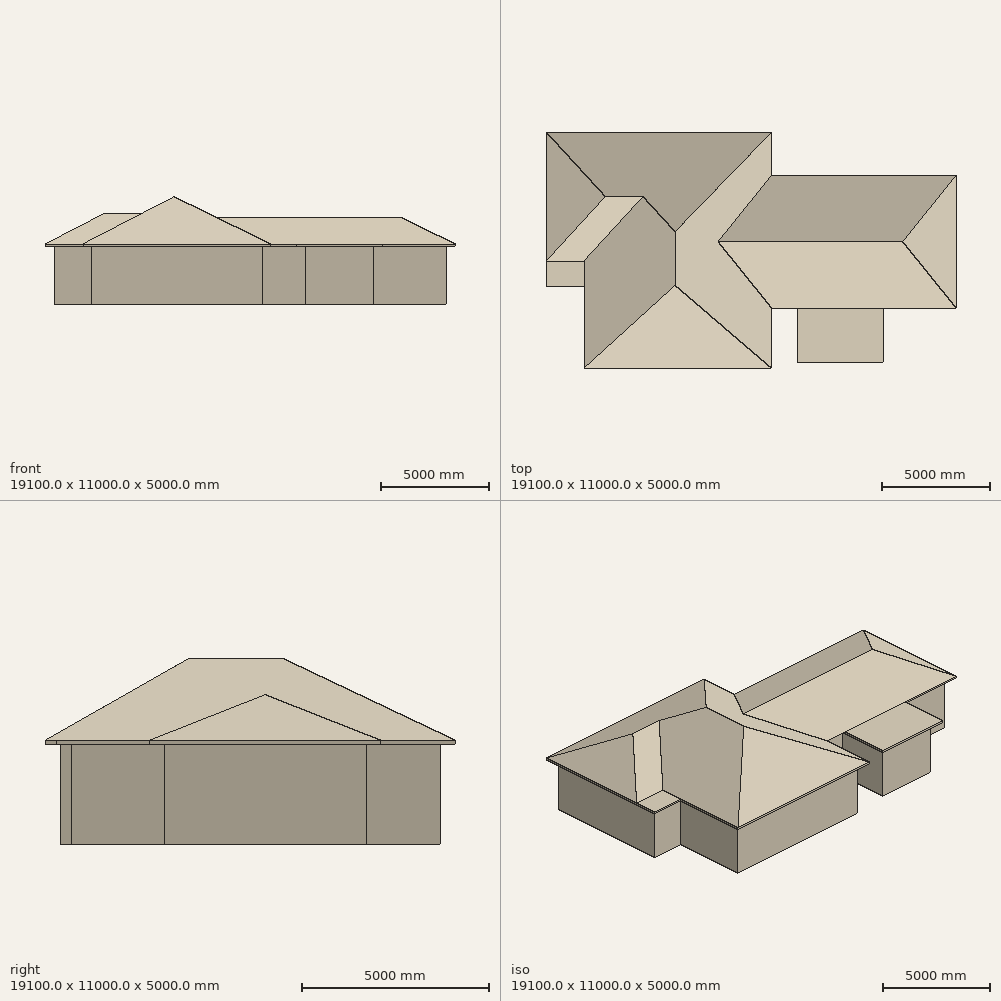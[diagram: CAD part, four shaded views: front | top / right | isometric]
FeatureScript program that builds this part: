
annotation { "Feature Type Name" : "Feature", "Feature Type Description" : "" }
export const myFeature = defineFeature(function(context is Context, id is Id, definition is map)
    precondition{}
    {
        {
            var Q0;
            Q0=qCreatedBy(makeId("Top.planeOp"),FACE);
            var sketch = newSketch(context, id + "F0", { "sketchPlane" : qUnion([Q0])});
            skLineSegment(sketch, "E0", {"start": v(0, 0) * mm, "end": v(10500, 0) * mm});
            skLineSegment(sketch, "E1", {"start": v(10500, 0) * mm, "end": v(10500, -2000) * mm});
            skLineSegment(sketch, "E2", {"start": v(10500, -2000) * mm, "end": v(19100, -2000) * mm});
            skLineSegment(sketch, "E3", {"start": v(19100, -2000) * mm, "end": v(19100, -8200) * mm});
            skLineSegment(sketch, "E4", {"start": v(19100, -8200) * mm, "end": v(15700, -8200) * mm});
            skLineSegment(sketch, "E5", {"start": v(15700, -8200) * mm, "end": v(15700, -10700) * mm});
            skLineSegment(sketch, "E6", {"start": v(15700, -10700) * mm, "end": v(11700, -10700) * mm});
            skLineSegment(sketch, "E7", {"start": v(11700, -10700) * mm, "end": v(11700, -8000) * mm});
            skLineSegment(sketch, "E8", {"start": v(11700, -8000) * mm, "end": v(10500, -8000) * mm});
            skLineSegment(sketch, "E9", {"start": v(10500, -8000) * mm, "end": v(10500, -11000) * mm});
            skLineSegment(sketch, "E10", {"start": v(10500, -11000) * mm, "end": v(1750, -11000) * mm});
            skLineSegment(sketch, "E11", {"start": v(0, -7200) * mm, "end": v(0, 0) * mm});
            skLineSegment(sketch, "E12", {"start": v(0, -7200) * mm, "end": v(1750, -7200) * mm});
            skLineSegment(sketch, "E13", {"start": v(1750, -7200) * mm, "end": v(1750, -11000) * mm});
            skLineSegment(sketch, "E14.0", {"start": v(400, -6800) * mm, "end": v(2150, -6800) * mm});
            skLineSegment(sketch, "E14.1", {"start": v(2150, -6800) * mm, "end": v(2150, -10600) * mm});
            skLineSegment(sketch, "E14.2", {"start": v(10100, -10600) * mm, "end": v(2150, -10600) * mm});
            skLineSegment(sketch, "E14.3", {"start": v(18700, -2400) * mm, "end": v(18700, -7800) * mm});
            skLineSegment(sketch, "E14.4", {"start": v(10100, -2400) * mm, "end": v(18700, -2400) * mm});
            skLineSegment(sketch, "E14.5", {"start": v(10100, -400) * mm, "end": v(10100, -2400) * mm});
            skLineSegment(sketch, "E14.6", {"start": v(400, -400) * mm, "end": v(10100, -400) * mm});
            skLineSegment(sketch, "E14.7", {"start": v(18700, -7800) * mm, "end": v(15300, -7800) * mm});
            skLineSegment(sketch, "E14.8", {"start": v(15300, -7800) * mm, "end": v(15300, -10300) * mm});
            skLineSegment(sketch, "E14.9", {"start": v(15300, -10300) * mm, "end": v(12100, -10300) * mm});
            skLineSegment(sketch, "E14.10", {"start": v(400, -6800) * mm, "end": v(400, -400) * mm});
            skLineSegment(sketch, "E14.11", {"start": v(12100, -10300) * mm, "end": v(12100, -7600) * mm});
            skLineSegment(sketch, "E14.12", {"start": v(12100, -7600) * mm, "end": v(10100, -7600) * mm});
            skLineSegment(sketch, "E14.13", {"start": v(10100, -7600) * mm, "end": v(10100, -10600) * mm});
            skLineSegment(sketch, "E15.0", {"start": v(500, -6700) * mm, "end": v(2250, -6700) * mm});
            skLineSegment(sketch, "E15.1", {"start": v(2250, -6700) * mm, "end": v(2250, -10500) * mm});
            skLineSegment(sketch, "E15.2", {"start": v(10000, -10500) * mm, "end": v(2250, -10500) * mm});
            skLineSegment(sketch, "E15.3", {"start": v(18600, -2500) * mm, "end": v(18600, -7700) * mm});
            skLineSegment(sketch, "E15.4", {"start": v(10000, -2500) * mm, "end": v(18600, -2500) * mm});
            skLineSegment(sketch, "E15.5", {"start": v(10000, -500) * mm, "end": v(10000, -2500) * mm});
            skLineSegment(sketch, "E15.6", {"start": v(500, -500) * mm, "end": v(10000, -500) * mm});
            skLineSegment(sketch, "E15.7", {"start": v(18600, -7700) * mm, "end": v(15200, -7700) * mm});
            skLineSegment(sketch, "E15.8", {"start": v(15200, -7700) * mm, "end": v(15200, -10200) * mm});
            skLineSegment(sketch, "E15.9", {"start": v(15200, -10200) * mm, "end": v(12200, -10200) * mm});
            skLineSegment(sketch, "E15.10", {"start": v(500, -6700) * mm, "end": v(500, -500) * mm});
            skLineSegment(sketch, "E15.11", {"start": v(12200, -10200) * mm, "end": v(12200, -7500) * mm});
            skLineSegment(sketch, "E15.12", {"start": v(12200, -7500) * mm, "end": v(10000, -7500) * mm});
            skLineSegment(sketch, "E15.13", {"start": v(10000, -7500) * mm, "end": v(10000, -10500) * mm});
            skSolve(sketch);
        }
        {
            var Q0;
            Q0=makeQuery(id+"F0.imprint","IMPRINT",FACE,{"disambiguationData":[TD([[makeQuery(id+"F0.imprint","IMPRINT",EDGE,{"derivedFrom":sQuery(id+"F0.wireOp",EDGE,"E14.0")}),1.0]])]});
            extrude(context, id + "F1", {"entities" : qUnion([Q0]), "depth" : 2700 * mm, "offsetDistance" : 25 * mm});
        }
        {
            var Q0;
            Q0=makeQuery(id+"F1.opExtrude","CAP_FACE",FACE,{"disambiguationData":[OSD([sQuery(id+"F0.wireOp",EDGE,"E14.0"),sQuery(id+"F0.wireOp",EDGE,"E14.1"),sQuery(id+"F0.wireOp",EDGE,"E14.2"),sQuery(id+"F0.wireOp",EDGE,"E14.3"),sQuery(id+"F0.wireOp",EDGE,"E14.4"),sQuery(id+"F0.wireOp",EDGE,"E14.5"),sQuery(id+"F0.wireOp",EDGE,"E14.6"),sQuery(id+"F0.wireOp",EDGE,"E14.7"),sQuery(id+"F0.wireOp",EDGE,"E14.8"),sQuery(id+"F0.wireOp",EDGE,"E14.9"),sQuery(id+"F0.wireOp",EDGE,"E14.10"),sQuery(id+"F0.wireOp",EDGE,"E14.11"),sQuery(id+"F0.wireOp",EDGE,"E14.12"),sQuery(id+"F0.wireOp",EDGE,"E14.13"),sQuery(id+"F0.wireOp",EDGE,"E15.0"),sQuery(id+"F0.wireOp",EDGE,"E15.1"),sQuery(id+"F0.wireOp",EDGE,"E15.2"),sQuery(id+"F0.wireOp",EDGE,"E15.3"),sQuery(id+"F0.wireOp",EDGE,"E15.4"),sQuery(id+"F0.wireOp",EDGE,"E15.5"),sQuery(id+"F0.wireOp",EDGE,"E15.6"),sQuery(id+"F0.wireOp",EDGE,"E15.7"),sQuery(id+"F0.wireOp",EDGE,"E15.8"),sQuery(id+"F0.wireOp",EDGE,"E15.9"),sQuery(id+"F0.wireOp",EDGE,"E15.10"),sQuery(id+"F0.wireOp",EDGE,"E15.11"),sQuery(id+"F0.wireOp",EDGE,"E15.12"),sQuery(id+"F0.wireOp",EDGE,"E15.13")])],"isStart":false});
            var sketch = newSketch(context, id + "F2", { "sketchPlane" : qUnion([Q0])});
            skLineSegment(sketch, "E16.0", {"start": v(10500, -11000) * mm, "end": v(1750, -11000) * mm});
            skLineSegment(sketch, "E17.0", {"start": v(1750, -7200) * mm, "end": v(1750, -11000) * mm});
            skLineSegment(sketch, "E18.0", {"start": v(0, -7200) * mm, "end": v(1750, -7200) * mm});
            skLineSegment(sketch, "E19.0", {"start": v(0, -7200) * mm, "end": v(0, 0) * mm});
            skLineSegment(sketch, "E20.0", {"start": v(0, 0) * mm, "end": v(10500, 0) * mm});
            skLineSegment(sketch, "E21.0", {"start": v(10500, 0) * mm, "end": v(10500, -2000) * mm});
            skLineSegment(sketch, "E22.0", {"start": v(10500, -2000) * mm, "end": v(19100, -2000) * mm});
            skLineSegment(sketch, "E23.0", {"start": v(19100, -2000) * mm, "end": v(19100, -8200) * mm});
            skLineSegment(sketch, "E24.0", {"start": v(19100, -8200) * mm, "end": v(15700, -8200) * mm});
            skLineSegment(sketch, "E25.0", {"start": v(15700, -8200) * mm, "end": v(15700, -10700) * mm});
            skLineSegment(sketch, "E26.0", {"start": v(15700, -10700) * mm, "end": v(11700, -10700) * mm});
            skLineSegment(sketch, "E27.0", {"start": v(11700, -10700) * mm, "end": v(11700, -8000) * mm});
            skLineSegment(sketch, "E28.0", {"start": v(11700, -8000) * mm, "end": v(10500, -8000) * mm});
            skLineSegment(sketch, "E29.0", {"start": v(10500, -8000) * mm, "end": v(10500, -11000) * mm});
            skSolve(sketch);
        }
        {
            var Q0;
            Q0=makeQuery(id+"F2.imprint","IMPRINT",FACE,{"disambiguationData":[TD([[makeQuery(id+"F2.imprint","IMPRINT",EDGE,{"derivedFrom":makeQuery(id+"F1.opExtrude","CAP_EDGE",EDGE,{"disambiguationData":[OSD([sQuery(id+"F0.wireOp",EDGE,"E15.0")])],"isStart":false})}),1.0]])]});
            var Q1;
            Q1=makeQuery(id+"F2.imprint","IMPRINT",FACE,{"disambiguationData":[TD([[makeQuery(id+"F2.imprint","IMPRINT",EDGE,{"derivedFrom":makeQuery(id+"F1.opExtrude","CAP_EDGE",EDGE,{"disambiguationData":[OSD([sQuery(id+"F0.wireOp",EDGE,"E14.0")])],"isStart":false})}),1.0]])]});
            var Q2;
            Q2=makeQuery(id+"F2.imprint","IMPRINT",FACE,{"disambiguationData":[TD([[makeQuery(id+"F2.imprint","IMPRINT",EDGE,{"derivedFrom":sQuery(id+"F2.wireOp",EDGE,"E16.0")}),-1.0]])]});
            extrude(context, id + "F3", {"entities" : qUnion([Q0, Q1, Q2]), "operationType" : NewBodyOperationType.ADD, "depth" : 100 * mm, "offsetDistance" : 25 * mm});
        }
        {
            var Q0;
            Q0=makeQuery(id+"F3.opExtrude","CAP_FACE",FACE,{"disambiguationData":[OSD([sQuery(id+"F2.wireOp",EDGE,"E16.0"),sQuery(id+"F2.wireOp",EDGE,"E17.0"),sQuery(id+"F2.wireOp",EDGE,"E18.0"),sQuery(id+"F2.wireOp",EDGE,"E19.0"),sQuery(id+"F2.wireOp",EDGE,"E20.0"),sQuery(id+"F2.wireOp",EDGE,"E21.0"),sQuery(id+"F2.wireOp",EDGE,"E22.0"),sQuery(id+"F2.wireOp",EDGE,"E23.0"),sQuery(id+"F2.wireOp",EDGE,"E24.0"),sQuery(id+"F2.wireOp",EDGE,"E25.0"),sQuery(id+"F2.wireOp",EDGE,"E26.0"),sQuery(id+"F2.wireOp",EDGE,"E27.0"),sQuery(id+"F2.wireOp",EDGE,"E28.0"),sQuery(id+"F2.wireOp",EDGE,"E29.0")])],"isStart":false});
            var sketch = newSketch(context, id + "F4", { "sketchPlane" : qUnion([Q0])});
            skLineSegment(sketch, "E30", {"start": v(6000, -4636.36) * mm, "end": v(6000, -7136.36) * mm});
            skLineSegment(sketch, "E31", {"start": v(0, -6000) * mm, "end": v(1750, -6000) * mm});
            skLineSegment(sketch, "E32", {"start": v(1750, -6000) * mm, "end": v(1750, -7200) * mm});
            skLineSegment(sketch, "E33", {"start": v(0, 0) * mm, "end": v(0, -6000) * mm});
            skLineSegment(sketch, "E34", {"start": v(0, -3000) * mm, "end": v(2750, -3000) * mm, "construction": true});
            skLineSegment(sketch, "E35", {"start": v(0, 0) * mm, "end": v(2750, -3000) * mm});
            skLineSegment(sketch, "E36", {"start": v(0, -6000) * mm, "end": v(2750, -3000) * mm});
            skLineSegment(sketch, "E37", {"start": v(1750, -6000) * mm, "end": v(4500, -3000) * mm});
            skLineSegment(sketch, "E38", {"start": v(2750, -3000) * mm, "end": v(4500, -3000) * mm});
            skLineSegment(sketch, "E39", {"start": v(4500, -3000) * mm, "end": v(6000, -4636.36) * mm});
            skLineSegment(sketch, "E40", {"start": v(1750, -6000) * mm, "end": v(1750, 0) * mm, "construction": true});
            skLineSegment(sketch, "E41", {"start": v(1750, 0) * mm, "end": v(6000, -4636.36) * mm, "construction": true});
            skLineSegment(sketch, "E42", {"start": v(6000, -4636.36) * mm, "end": v(10500, 0) * mm});
            skLineSegment(sketch, "E43", {"start": v(1750, -11000) * mm, "end": v(6000, -7136.36) * mm});
            skLineSegment(sketch, "E44", {"start": v(10500, -11000) * mm, "end": v(6000, -7136.36) * mm});
            skLineSegment(sketch, "E45", {"start": v(19100, -5100) * mm, "end": v(16600, -5100) * mm, "construction": true});
            skLineSegment(sketch, "E46", {"start": v(19100, -2000) * mm, "end": v(16600, -5100) * mm});
            skLineSegment(sketch, "E47", {"start": v(19100, -8200) * mm, "end": v(16600, -5100) * mm});
            skLineSegment(sketch, "E48", {"start": v(10500, -2000) * mm, "end": v(8000, -5100) * mm});
            skLineSegment(sketch, "E49", {"start": v(8000, -5100) * mm, "end": v(10500, -8000) * mm});
            skLineSegment(sketch, "E50", {"start": v(8000, -5100) * mm, "end": v(16600, -5100) * mm});
            skSolve(sketch);
        }
        {
            var Q0;
            Q0=qCreatedBy(makeId("Right.planeOp"),FACE);
            var Q1;
            Q1=sQuery(id+"F4.wireOp",EDGE,"E30");
            cPlane(context, id + "F5", {"entities" : qUnion([Q0, Q1]), "cplaneType" : CPlaneType.LINE_ANGLE, "offset" : 25 * mm, "angle" : 0 * degree, "width" : 150 * mm, "height" : 150 * mm});
        }
        {
            var Q0;
            Q0=qCreatedBy(id+"F5.planeOp",FACE);
            var sketch = newSketch(context, id + "F6", { "sketchPlane" : qUnion([Q0])});
            skPoint(sketch, "E51.0", {"position": v(4636.36, 2800) * mm});
            skPoint(sketch, "E52.0", {"position": v(7136.36, 2800) * mm});
            skLineSegment(sketch, "E53", {"start": v(7136.36, 2800) * mm, "end": v(7136.36, 5000) * mm});
            skLineSegment(sketch, "E54", {"start": v(7136.36, 5000) * mm, "end": v(4636.36, 5000) * mm});
            skLineSegment(sketch, "E55", {"start": v(4636.36, 5000) * mm, "end": v(4636.36, 2800) * mm});
            skSolve(sketch);
        }
        {
            var Q0;
            Q0=sQuery(id+"F6.wireOp",VERTEX,"E55.start");
            var Q1;
            Q1=sQuery(id+"F4.wireOp",VERTEX,"E42.end");
            var Q2;
            Q2=sQuery(id+"F4.wireOp",VERTEX,"E35.start");
            cPlane(context, id + "F7", {"entities" : qUnion([Q0, Q1, Q2]), "cplaneType" : CPlaneType.THREE_POINT, "offset" : 25 * mm, "width" : 150 * mm, "height" : 150 * mm});
        }
        {
            var Q0;
            Q0=qCreatedBy(makeId("Front.planeOp"),FACE);
            var Q1;
            Q1=sQuery(id+"F4.wireOp",EDGE,"E38");
            cPlane(context, id + "F8", {"entities" : qUnion([Q0, Q1]), "cplaneType" : CPlaneType.LINE_ANGLE, "offset" : 25 * mm, "angle" : 0 * degree, "width" : 150 * mm, "height" : 150 * mm});
        }
        {
            var Q0;
            Q0=qCreatedBy(id+"F8.planeOp",FACE);
            var sketch = newSketch(context, id + "F9", { "sketchPlane" : qUnion([Q0])});
            skPoint(sketch, "E56.0", {"position": v(-2750, 2800) * mm});
            skPoint(sketch, "E57.0", {"position": v(-4500, 2800) * mm});
            skLineSegment(sketch, "E58", {"start": v(-2750, 2800) * mm, "end": v(-2750, 5373.06) * mm});
            skLineSegment(sketch, "E59", {"start": v(-4500, 2800) * mm, "end": v(-4500, 5035.9) * mm});
            skSolve(sketch);
        }
        {
            var Q0;
            Q0=qCreatedBy(id+"F7.planeOp",FACE);
            var sketch = newSketch(context, id + "F10", { "sketchPlane" : qUnion([Q0])});
            skPoint(sketch, "E60.0", {"position": v(10500, 1200.35) * mm});
            skPoint(sketch, "E61.0", {"position": v(6000, 6332.2) * mm});
            skPoint(sketch, "E62.0", {"position": v(4500, 3910.7) * mm});
            skPoint(sketch, "E63.0", {"position": v(2750, 3910.7) * mm});
            skPoint(sketch, "E64.0", {"position": v(0, 1200.35) * mm});
            skLineSegment(sketch, "E65", {"start": v(10500, 1200.35) * mm, "end": v(6000, 6332.2) * mm});
            skLineSegment(sketch, "E66", {"start": v(10500, 1200.35) * mm, "end": v(0, 1200.35) * mm});
            skLineSegment(sketch, "E67.0", {"start": v(4500, 3910.7) * mm, "end": v(4500, 4869.22) * mm});
            skLineSegment(sketch, "E68.0", {"start": v(2750, 3910.7) * mm, "end": v(2750, 5013.75) * mm});
            skLineSegment(sketch, "E69", {"start": v(0, 1200.35) * mm, "end": v(2750, 4520.96) * mm});
            skLineSegment(sketch, "E70", {"start": v(2750, 4520.96) * mm, "end": v(4500, 4520.96) * mm});
            skLineSegment(sketch, "E71", {"start": v(4500, 4520.96) * mm, "end": v(6000, 6332.2) * mm});
            skSolve(sketch);
        }
        {
            var Q0;
            Q0=makeQuery(id+"F10.imprint","IMPRINT",FACE,{"disambiguationData":[TD([[makeQuery(id+"F10.imprint","IMPRINT",EDGE,{"derivedFrom":sQuery(id+"F10.wireOp",EDGE,"E65")}),1.0]])]});
            extrude(context, id + "F11", {"entities" : qUnion([Q0]), "operationType" : NewBodyOperationType.ADD, "depth" : 25 * mm, "offsetDistance" : 25 * mm});
        }
        {
            var Q0;
            Q0=sQuery(id+"F4.wireOp",VERTEX,"E43.start");
            var Q1;
            Q1=sQuery(id+"F6.wireOp",VERTEX,"E53.end");
            var Q2;
            Q2=sQuery(id+"F4.wireOp",VERTEX,"E44.start");
            cPlane(context, id + "F12", {"entities" : qUnion([Q0, Q1, Q2]), "cplaneType" : CPlaneType.THREE_POINT, "offset" : 25 * mm, "width" : 150 * mm, "height" : 150 * mm});
        }
        {
            var Q0;
            Q0=qCreatedBy(id+"F12.planeOp",FACE);
            var sketch = newSketch(context, id + "F13", { "sketchPlane" : qUnion([Q0])});
            skPoint(sketch, "E72.0", {"position": v(1750, -8173.48) * mm});
            skPoint(sketch, "E73.0", {"position": v(6000, -3727.4) * mm});
            skPoint(sketch, "E74.0", {"position": v(10500, -8173.48) * mm});
            skLineSegment(sketch, "E75", {"start": v(1750, -8173.48) * mm, "end": v(6000, -3727.4) * mm});
            skLineSegment(sketch, "E76", {"start": v(10500, -8173.48) * mm, "end": v(6000, -3727.4) * mm});
            skLineSegment(sketch, "E77", {"start": v(10500, -8173.48) * mm, "end": v(1750, -8173.48) * mm});
            skSolve(sketch);
        }
        {
            var Q0;
            Q0=makeQuery(id+"F13.imprint","IMPRINT",FACE,{"disambiguationData":[TD([[makeQuery(id+"F13.imprint","IMPRINT",EDGE,{"derivedFrom":sQuery(id+"F13.wireOp",EDGE,"E75")}),-1.0]])]});
            extrude(context, id + "F14", {"entities" : qUnion([Q0]), "oppositeDirection" : true, "depth" : 25 * mm, "offsetDistance" : 25 * mm});
        }
        {
            var Q0;
            Q0=sQuery(id+"F4.wireOp",VERTEX,"E35.start");
            var Q1;
            Q1=sQuery(id+"F4.wireOp",VERTEX,"E36.start");
            var Q2;
            Q2=makeQuery(id+"F11.opExtrude","CAP_VERTEX",VERTEX,{"disambiguationData":[OSD([sQuery(id+"F10.wireOp",EDGE,"E69"),sQuery(id+"F10.wireOp",EDGE,"E70")])],"isStart":true});
            cPlane(context, id + "F15", {"entities" : qUnion([Q0, Q1, Q2]), "cplaneType" : CPlaneType.THREE_POINT, "offset" : 25 * mm, "width" : 150 * mm, "height" : 150 * mm});
        }
        {
            var Q0;
            Q0=qCreatedBy(id+"F15.planeOp",FACE);
            var sketch = newSketch(context, id + "F16", { "sketchPlane" : qUnion([Q0])});
            skPoint(sketch, "E78.0", {"position": v(1287.18, 0) * mm});
            skPoint(sketch, "E79.0", {"position": v(1287.18, 6000) * mm});
            skPoint(sketch, "E80.0", {"position": v(4383.78, 3000) * mm});
            skLineSegment(sketch, "E81", {"start": v(1287.18, 0) * mm, "end": v(4383.78, 3000) * mm});
            skLineSegment(sketch, "E82", {"start": v(1287.18, 6000) * mm, "end": v(4383.78, 3000) * mm});
            skLineSegment(sketch, "E83", {"start": v(1287.18, 6000) * mm, "end": v(1287.18, 0) * mm});
            skSolve(sketch);
        }
        {
            var Q0;
            Q0=makeQuery(id+"F16.imprint","IMPRINT",FACE,{"disambiguationData":[TD([[makeQuery(id+"F16.imprint","IMPRINT",EDGE,{"derivedFrom":sQuery(id+"F16.wireOp",EDGE,"E81")}),1.0]])]});
            extrude(context, id + "F17", {"entities" : qUnion([Q0]), "operationType" : NewBodyOperationType.ADD, "depth" : 25 * mm, "offsetDistance" : 25 * mm});
        }
        {
            var Q0;
            Q0=sQuery(id+"F4.wireOp",VERTEX,"E36.start");
            var Q1;
            Q1=sQuery(id+"F4.wireOp",VERTEX,"E32.start");
            var Q2;
            Q2=makeQuery(id+"F11.opExtrude","CAP_VERTEX",VERTEX,{"disambiguationData":[OSD([sQuery(id+"F10.wireOp",EDGE,"E70"),sQuery(id+"F10.wireOp",EDGE,"E71")])],"isStart":true});
            cPlane(context, id + "F18", {"entities" : qUnion([Q0, Q1, Q2]), "cplaneType" : CPlaneType.THREE_POINT, "offset" : 25 * mm, "width" : 150 * mm, "height" : 150 * mm});
        }
        {
            var Q0;
            Q0=qCreatedBy(id+"F18.planeOp",FACE);
            var sketch = newSketch(context, id + "F19", { "sketchPlane" : qUnion([Q0])});
            skPoint(sketch, "E84.0", {"position": v(0, 4220.35) * mm});
            skPoint(sketch, "E85.0", {"position": v(1750, 4220.35) * mm});
            skLineSegment(sketch, "E86.0", {"start": v(2750, 899.74) * mm, "end": v(4500, 899.74) * mm});
            skLineSegment(sketch, "E87", {"start": v(4500, 899.74) * mm, "end": v(1750, 4220.35) * mm});
            skLineSegment(sketch, "E88", {"start": v(1750, 4220.35) * mm, "end": v(0, 4220.35) * mm});
            skLineSegment(sketch, "E89", {"start": v(0, 4220.35) * mm, "end": v(2750, 899.74) * mm});
            skSolve(sketch);
        }
        {
            var Q0;
            Q0=makeQuery(id+"F19.imprint","IMPRINT",FACE,{"disambiguationData":[TD([[makeQuery(id+"F19.imprint","IMPRINT",EDGE,{"derivedFrom":sQuery(id+"F19.wireOp",EDGE,"E86.0")}),1.0]])]});
            extrude(context, id + "F20", {"entities" : qUnion([Q0]), "operationType" : NewBodyOperationType.ADD, "depth" : 25 * mm, "offsetDistance" : 25 * mm});
        }
        {
            var Q0;
            Q0=sQuery(id+"F4.wireOp",VERTEX,"E43.start");
            var Q1;
            Q1=sQuery(id+"F6.wireOp",VERTEX,"E54.start");
            var Q2;
            Q2=sQuery(id+"F4.wireOp",VERTEX,"E32.start");
            cPlane(context, id + "F21", {"entities" : qUnion([Q0, Q1, Q2]), "cplaneType" : CPlaneType.THREE_POINT, "offset" : 25 * mm, "width" : 150 * mm, "height" : 150 * mm});
        }
        {
            var Q0;
            Q0=qCreatedBy(id+"F21.planeOp",FACE);
            var sketch = newSketch(context, id + "F22", { "sketchPlane" : qUnion([Q0])});
            skLineSegment(sketch, "E90.0", {"start": v(7626.96, 7136.36) * mm, "end": v(7626.96, 4636.36) * mm});
            skLineSegment(sketch, "E91.0", {"start": v(2841.3, 11000) * mm, "end": v(7626.96, 7136.36) * mm});
            skLineSegment(sketch, "E92.0", {"start": v(5937.9, 3000) * mm, "end": v(2841.3, 6000) * mm});
            skLineSegment(sketch, "E93.0", {"start": v(5937.9, 3000) * mm, "end": v(7626.96, 4636.36) * mm});
            skLineSegment(sketch, "E94.0", {"start": v(2841.3, 6000) * mm, "end": v(2841.3, 7200) * mm});
            skLineSegment(sketch, "E95.0", {"start": v(2841.3, 7200) * mm, "end": v(2841.3, 11000) * mm});
            skSolve(sketch);
        }
        {
            var Q0;
            Q0=makeQuery(id+"F22.imprint","IMPRINT",FACE,{"disambiguationData":[TD([[makeQuery(id+"F22.imprint","IMPRINT",EDGE,{"derivedFrom":sQuery(id+"F22.wireOp",EDGE,"E90.0")}),-1.0]])]});
            extrude(context, id + "F23", {"entities" : qUnion([Q0]), "depth" : 25 * mm, "offsetDistance" : 25 * mm});
        }
        {
            var Q0;
            Q0=sQuery(id+"F4.wireOp",VERTEX,"E44.start");
            var Q1;
            Q1=sQuery(id+"F4.wireOp",VERTEX,"E42.end");
            var Q2;
            Q2=sQuery(id+"F6.wireOp",VERTEX,"E55.start");
            cPlane(context, id + "F24", {"entities" : qUnion([Q0, Q1, Q2]), "cplaneType" : CPlaneType.THREE_POINT, "offset" : 25 * mm, "width" : 150 * mm, "height" : 150 * mm});
        }
        {
            var Q0;
            Q0=qCreatedBy(id+"F24.planeOp",FACE);
            var sketch = newSketch(context, id + "F25", { "sketchPlane" : qUnion([Q0])});
            skPoint(sketch, "E96.0", {"position": v(8203.25, 11000) * mm});
            skPoint(sketch, "E97.0", {"position": v(8203.25, 0) * mm});
            skPoint(sketch, "E98.0", {"position": v(3194.26, 4636.36) * mm});
            skPoint(sketch, "E99.0", {"position": v(3194.26, 7136.36) * mm});
            skLineSegment(sketch, "E100", {"start": v(8203.25, 11000) * mm, "end": v(3194.26, 7136.36) * mm});
            skLineSegment(sketch, "E101", {"start": v(3194.26, 7136.36) * mm, "end": v(3194.26, 4636.36) * mm});
            skLineSegment(sketch, "E102", {"start": v(3194.26, 4636.36) * mm, "end": v(8203.25, 0) * mm});
            skLineSegment(sketch, "E103", {"start": v(8203.25, 0) * mm, "end": v(8203.25, 11000) * mm});
            skSolve(sketch);
        }
        {
            var Q0;
            Q0=makeQuery(id+"F25.imprint","IMPRINT",FACE,{"disambiguationData":[TD([[makeQuery(id+"F25.imprint","IMPRINT",EDGE,{"derivedFrom":sQuery(id+"F25.wireOp",EDGE,"E100")}),1.0]])]});
            extrude(context, id + "F26", {"entities" : qUnion([Q0]), "depth" : 25 * mm, "offsetDistance" : 25 * mm});
        }
        {
            var Q0;
            Q0=sQuery(id+"F4.wireOp",EDGE,"E50");
            var Q1;
            Q1=qCreatedBy(makeId("Front.planeOp"),FACE);
            cPlane(context, id + "F27", {"entities" : qUnion([Q0, Q1]), "cplaneType" : CPlaneType.LINE_ANGLE, "offset" : 25 * mm, "angle" : 0 * degree, "width" : 150 * mm, "height" : 150 * mm});
        }
        {
            var Q0;
            Q0=qCreatedBy(id+"F27.planeOp",FACE);
            var sketch = newSketch(context, id + "F28", { "sketchPlane" : qUnion([Q0])});
            skPoint(sketch, "E104.0", {"position": v(-8000, 2800) * mm});
            skLineSegment(sketch, "E105.0.0", {"start": v(-10500, 2800) * mm, "end": v(-6000, 5000) * mm});
            skLineSegment(sketch, "E105.0.2", {"start": v(-6000, 5000) * mm, "end": v(-10500, 2800) * mm});
            skLineSegment(sketch, "E106", {"start": v(-8000, 2800) * mm, "end": v(-8000, 4022.22) * mm, "construction": true});
            skLineSegment(sketch, "E107", {"start": v(-8000, 4022.22) * mm, "end": v(-16600, 4022.22) * mm, "construction": true});
            skPoint(sketch, "E108.0", {"position": v(-16600, 2800) * mm});
            skLineSegment(sketch, "E109", {"start": v(-16600, 2800) * mm, "end": v(-16600, 4022.22) * mm});
            skSolve(sketch);
        }
        {
            var Q0;
            Q0=sQuery(id+"F4.wireOp",VERTEX,"E46.start");
            var Q1;
            Q1=sQuery(id+"F28.wireOp",VERTEX,"E107.end");
            var Q2;
            Q2=sQuery(id+"F28.wireOp",VERTEX,"E107.start");
            cPlane(context, id + "F29", {"entities" : qUnion([Q0, Q1, Q2]), "cplaneType" : CPlaneType.THREE_POINT, "offset" : 25 * mm, "width" : 150 * mm, "height" : 150 * mm});
        }
        {
            var Q0;
            Q0=qCreatedBy(id+"F29.planeOp",FACE);
            var sketch = newSketch(context, id + "F30", { "sketchPlane" : qUnion([Q0])});
            skPoint(sketch, "E110.0", {"position": v(19100, -2887.61) * mm});
            skLineSegment(sketch, "E111.0", {"start": v(10500, -2887.61) * mm, "end": v(19100, -2887.61) * mm});
            skPoint(sketch, "E112.0", {"position": v(16600, -6219.85) * mm});
            skPoint(sketch, "E113.0", {"position": v(8000, -6219.85) * mm});
            skLineSegment(sketch, "E114", {"start": v(19100, -2887.61) * mm, "end": v(16600, -6219.85) * mm});
            skLineSegment(sketch, "E115", {"start": v(16600, -6219.85) * mm, "end": v(8000, -6219.85) * mm});
            skLineSegment(sketch, "E116", {"start": v(8000, -6219.85) * mm, "end": v(10500, -2887.61) * mm});
            skSolve(sketch);
        }
        {
            var Q0;
            Q0=makeQuery(id+"F30.imprint","IMPRINT",FACE,{"disambiguationData":[TD([[makeQuery(id+"F30.imprint","IMPRINT",EDGE,{"derivedFrom":sQuery(id+"F30.wireOp",EDGE,"E111.0")}),-1.0]])]});
            extrude(context, id + "F31", {"entities" : qUnion([Q0]), "oppositeDirection" : true, "depth" : 25 * mm, "offsetDistance" : 25 * mm});
        }
        {
            var Q0;
            Q0=sQuery(id+"F28.wireOp",VERTEX,"E109.end");
            var Q1;
            Q1=sQuery(id+"F28.wireOp",VERTEX,"E107.start");
            var Q2;
            Q2=sQuery(id+"F4.wireOp",VERTEX,"E47.start");
            cPlane(context, id + "F32", {"entities" : qUnion([Q0, Q1, Q2]), "cplaneType" : CPlaneType.THREE_POINT, "offset" : 25 * mm, "width" : 150 * mm, "height" : 150 * mm});
        }
        {
            var Q0;
            Q0=qCreatedBy(id+"F32.planeOp",FACE);
            var sketch = newSketch(context, id + "F33", { "sketchPlane" : qUnion([Q0])});
            skPoint(sketch, "E117.0", {"position": v(8000, 3269.26) * mm});
            skPoint(sketch, "E118.0", {"position": v(16600, 3269.26) * mm});
            skPoint(sketch, "E119.0", {"position": v(19100, 6601.5) * mm});
            skLineSegment(sketch, "E120.0", {"start": v(10500, 6415.44) * mm, "end": v(10500, 9206.35) * mm});
            skLineSegment(sketch, "E121", {"start": v(8000, 3269.26) * mm, "end": v(16600, 3269.26) * mm});
            skLineSegment(sketch, "E122", {"start": v(16600, 3269.26) * mm, "end": v(19100, 6601.5) * mm});
            skLineSegment(sketch, "E123", {"start": v(19100, 6601.5) * mm, "end": v(10500, 6601.5) * mm});
            skLineSegment(sketch, "E124", {"start": v(10500, 6601.5) * mm, "end": v(8000, 3269.26) * mm});
            skSolve(sketch);
        }
        {
            var Q0;
            Q0=makeQuery(id+"F33.imprint","IMPRINT",FACE,{"disambiguationData":[TD([[makeQuery(id+"F33.imprint","IMPRINT",EDGE,{"derivedFrom":sQuery(id+"F33.wireOp",EDGE,"E121")}),1.0]])]});
            extrude(context, id + "F34", {"entities" : qUnion([Q0]), "depth" : 25 * mm, "offsetDistance" : 25 * mm});
        }
        {
            var Q0;
            Q0=sQuery(id+"F28.wireOp",VERTEX,"E109.end");
            var Q1;
            Q1=sQuery(id+"F4.wireOp",VERTEX,"E47.start");
            var Q2;
            Q2=sQuery(id+"F4.wireOp",VERTEX,"E46.start");
            cPlane(context, id + "F35", {"entities" : qUnion([Q0, Q1, Q2]), "cplaneType" : CPlaneType.THREE_POINT, "offset" : 25 * mm, "width" : 150 * mm, "height" : 150 * mm});
        }
        {
            var Q0;
            Q0=qCreatedBy(id+"F35.planeOp",FACE);
            var sketch = newSketch(context, id + "F36", { "sketchPlane" : qUnion([Q0])});
            skLineSegment(sketch, "E125.0", {"start": v(13146.58, 5100) * mm, "end": v(15929.35, 8200) * mm});
            skLineSegment(sketch, "E126.0", {"start": v(15929.35, 2000) * mm, "end": v(13146.58, 5100) * mm});
            skLineSegment(sketch, "E127.0", {"start": v(15929.35, 2000) * mm, "end": v(15929.35, 8200) * mm});
            skSolve(sketch);
        }
        {
            var Q0;
            Q0=makeQuery(id+"F36.imprint","IMPRINT",FACE,{"disambiguationData":[TD([[makeQuery(id+"F36.imprint","IMPRINT",EDGE,{"derivedFrom":sQuery(id+"F36.wireOp",EDGE,"E125.0")}),-1.0]])]});
            extrude(context, id + "F37", {"entities" : qUnion([Q0]), "depth" : 25 * mm, "offsetDistance" : 25 * mm});
        }
    });
